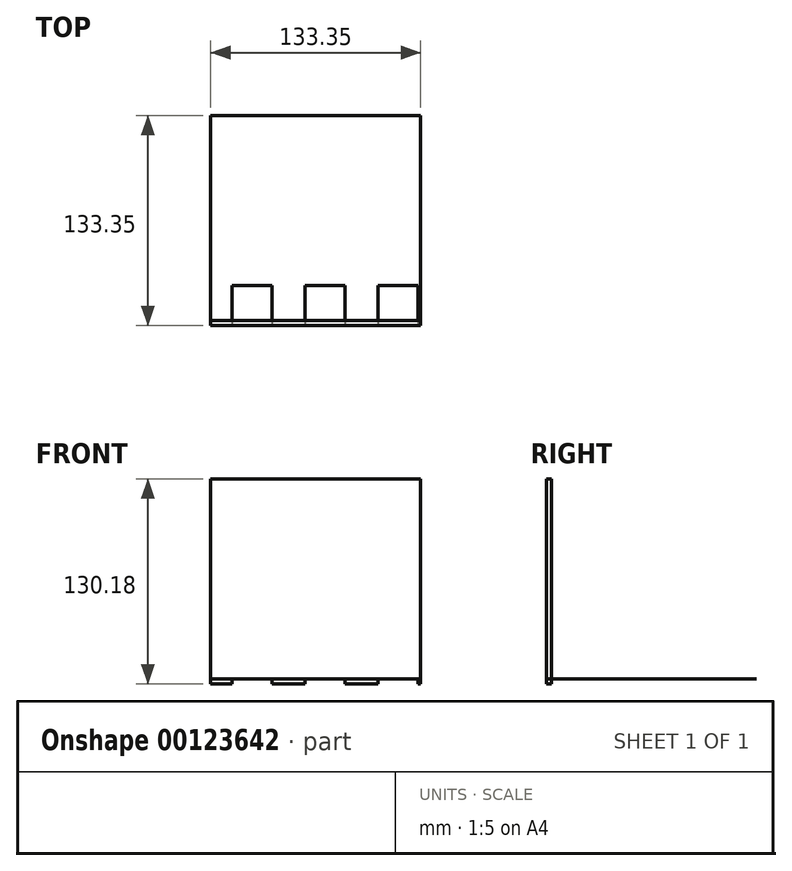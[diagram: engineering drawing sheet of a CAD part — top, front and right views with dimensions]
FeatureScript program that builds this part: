
annotation { "Feature Type Name" : "Feature", "Feature Type Description" : "" }
export const myFeature = defineFeature(function(context is Context, id is Id, definition is map)
    precondition{}
    {
        {
            var Q0;
            Q0=qCreatedBy(makeId("Top.planeOp"),FACE);
            var sketch = newSketch(context, id + "F0", { "sketchPlane" : qUnion([Q0])});
            skLineSegment(sketch, "E0.bottom", {"start": v(-62.68, 67.86) * mm, "end": v(70.67, 67.86) * mm});
            skLineSegment(sketch, "E0.top", {"start": v(-62.68, -65.49) * mm, "end": v(70.67, -65.49) * mm});
            skLineSegment(sketch, "E0.left", {"start": v(-62.68, 67.86) * mm, "end": v(-62.68, -65.49) * mm});
            skLineSegment(sketch, "E0.right", {"start": v(70.67, 67.86) * mm, "end": v(70.67, -65.49) * mm});
            skSolve(sketch);
        }
        {
            var Q0;
            Q0=makeQuery(id+"F0.imprint","IMPRINT",FACE,{"disambiguationData":[TD([[makeQuery(id+"F0.imprint","IMPRINT",EDGE,{"derivedFrom":sQuery(id+"F0.wireOp",EDGE,"E0.bottom")}),-1.0]])]});
            extrude(context, id + "F1", {"entities" : qUnion([Q0]), "oppositeDirection" : true, "depth" : 1 / 203.2 * mm});
        }
        {
            var Q0;
            Q0=qCreatedBy(makeId("Top.planeOp"),FACE);
            var sketch = newSketch(context, id + "F2", { "sketchPlane" : qUnion([Q0])});
            skLineSegment(sketch, "E1.bottom", {"start": v(-62.68, -62.31) * mm, "end": v(70.67, -62.31) * mm});
            skLineSegment(sketch, "E1.top", {"start": v(-62.68, -65.49) * mm, "end": v(70.67, -65.49) * mm});
            skLineSegment(sketch, "E1.left", {"start": v(-62.68, -62.31) * mm, "end": v(-62.68, -65.49) * mm});
            skLineSegment(sketch, "E1.right", {"start": v(70.67, -62.31) * mm, "end": v(70.67, -65.49) * mm});
            skSolve(sketch);
        }
        {
            var Q0;
            Q0 = qSketchRegion(id + "F2", true);
            extrude(context, id + "F3", {"entities" : qUnion([Q0]), "depth" : 127 * mm, "hasSecondDirection" : true, "secondDirectionOppositeDirection" : true, "secondDirectionDepth" : 3.17 * mm});
        }
        {
            var Q0;
            Q0=makeQuery(id+"F1.opExtrude","SWEPT_FACE",FACE,{"disambiguationData":[OSD([sQuery(id+"F0.wireOp",EDGE,"E0.top")])]});
            var sketch = newSketch(context, id + "F4", { "sketchPlane" : qUnion([Q0])});
            skLineSegment(sketch, "E2", {"start": v(-49.3, -3.18) * mm, "end": v(-49.3, 0) * mm});
            skLineSegment(sketch, "E3", {"start": v(-49.3, 0) * mm, "end": v(-23.9, 0) * mm});
            skLineSegment(sketch, "E4", {"start": v(-23.9, 0) * mm, "end": v(-23.9, -3.17) * mm});
            skLineSegment(sketch, "E5", {"start": v(-23.9, -3.18) * mm, "end": v(-49.3, -3.18) * mm});
            skLineSegment(sketch, "E6", {"start": v(-2.94, -3.17) * mm, "end": v(-2.94, 0) * mm});
            skLineSegment(sketch, "E7", {"start": v(-2.94, 0) * mm, "end": v(22.46, 0) * mm});
            skLineSegment(sketch, "E8", {"start": v(22.46, 0) * mm, "end": v(22.46, -3.17) * mm});
            skLineSegment(sketch, "E9", {"start": v(22.46, -3.18) * mm, "end": v(-2.94, -3.18) * mm});
            skLineSegment(sketch, "E10", {"start": v(43.42, -3.17) * mm, "end": v(43.42, 0) * mm});
            skLineSegment(sketch, "E11", {"start": v(43.42, 0) * mm, "end": v(68.82, 0) * mm});
            skLineSegment(sketch, "E12", {"start": v(68.82, 0) * mm, "end": v(68.82, -3.17) * mm});
            skLineSegment(sketch, "E13", {"start": v(68.82, -3.18) * mm, "end": v(43.42, -3.18) * mm});
            skSolve(sketch);
        }
        {
            var Q0;
            Q0=makeQuery(id+"F4.imprint","IMPRINT",FACE,{"disambiguationData":[TD([[makeQuery(id+"F4.imprint","IMPRINT",EDGE,{"derivedFrom":sQuery(id+"F4.wireOp",EDGE,"E2")}),-1.0]])]});
            var Q1;
            Q1=makeQuery(id+"F4.imprint","IMPRINT",FACE,{"disambiguationData":[TD([[makeQuery(id+"F4.imprint","IMPRINT",EDGE,{"derivedFrom":sQuery(id+"F4.wireOp",EDGE,"E6")}),-1.0]])]});
            var Q2;
            Q2=makeQuery(id+"F4.imprint","IMPRINT",FACE,{"disambiguationData":[TD([[makeQuery(id+"F4.imprint","IMPRINT",EDGE,{"derivedFrom":sQuery(id+"F4.wireOp",EDGE,"E10")}),-1.0]])]});
            extrude(context, id + "F5", {"entities" : qUnion([Q0, Q1, Q2]), "operationType" : NewBodyOperationType.REMOVE, "oppositeDirection" : true, "depth" : 25.4 * mm});
        }
    });
